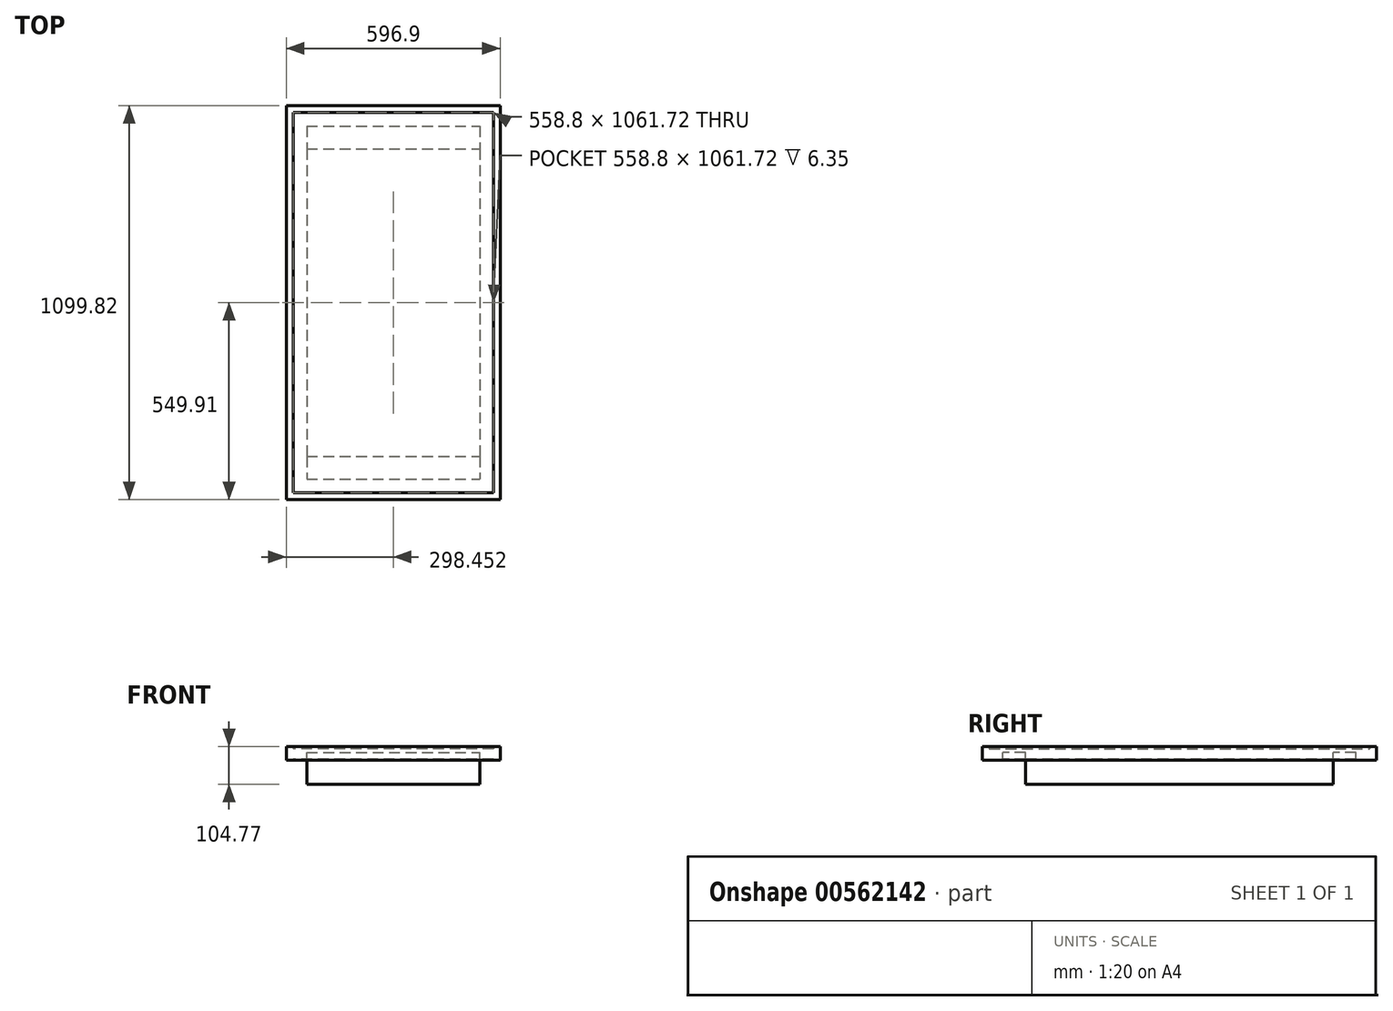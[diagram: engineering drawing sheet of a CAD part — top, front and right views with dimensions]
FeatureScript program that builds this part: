
annotation { "Feature Type Name" : "Feature", "Feature Type Description" : "" }
export const myFeature = defineFeature(function(context is Context, id is Id, definition is map)
    precondition{}
    {
        {
            var Q0;
            Q0=qCreatedBy(makeId("Top.planeOp"),FACE);
            var sketch = newSketch(context, id + "F0", { "sketchPlane" : qUnion([Q0])});
            skLineSegment(sketch, "E0.bottom", {"start": v(-98.88, 1025.28) * mm, "end": v(498.02, 1025.28) * mm});
            skLineSegment(sketch, "E0.top", {"start": v(-98.88, -74.54) * mm, "end": v(498.02, -74.54) * mm});
            skLineSegment(sketch, "E0.left", {"start": v(-98.88, 1025.28) * mm, "end": v(-98.88, -74.54) * mm});
            skLineSegment(sketch, "E0.right", {"start": v(498.02, 1025.28) * mm, "end": v(498.02, -74.54) * mm});
            skLineSegment(sketch, "E1.bottom", {"start": v(-79.83, 1006.23) * mm, "end": v(478.97, 1006.23) * mm});
            skLineSegment(sketch, "E1.top", {"start": v(-79.83, -55.5) * mm, "end": v(478.97, -55.5) * mm});
            skLineSegment(sketch, "E1.left", {"start": v(-79.83, 1006.23) * mm, "end": v(-79.83, -55.5) * mm});
            skLineSegment(sketch, "E1.right", {"start": v(478.97, 1006.23) * mm, "end": v(478.97, -55.5) * mm});
            skSolve(sketch);
        }
        {
            var Q0;
            Q0=makeQuery(id+"F0.imprint","IMPRINT",FACE,{"disambiguationData":[TD([[makeQuery(id+"F0.imprint","IMPRINT",EDGE,{"derivedFrom":sQuery(id+"F0.wireOp",EDGE,"E0.bottom")}),-1.0]])]});
            extrude(context, id + "F1", {"entities" : qUnion([Q0]), "depth" : 38.1 * mm, "offsetDistance" : 25.4 * mm});
        }
        {
            var Q0;
            Q0=makeQuery(id+"F1.opExtrude","SWEPT_FACE",FACE,{"disambiguationData":[OSD([sQuery(id+"F0.wireOp",EDGE,"E0.left")])]});
            var sketch = newSketch(context, id + "F2", { "sketchPlane" : qUnion([Q0])});
            skLineSegment(sketch, "E2.bottom", {"start": v(-1025.28, 31.75) * mm, "end": v(74.54, 31.75) * mm});
            skLineSegment(sketch, "E2.top", {"start": v(-1025.28, 22.23) * mm, "end": v(74.54, 22.23) * mm});
            skLineSegment(sketch, "E2.left", {"start": v(-1025.28, 31.75) * mm, "end": v(-1025.28, 22.23) * mm});
            skLineSegment(sketch, "E2.right", {"start": v(74.54, 31.75) * mm, "end": v(74.54, 22.23) * mm});
            skSolve(sketch);
        }
        {
            var Q0;
            Q0 = qSketchRegion(id + "F2", true);
            extrude(context, id + "F3", {"entities" : qUnion([Q0]), "operationType" : NewBodyOperationType.ADD, "oppositeDirection" : true, "depth" : 584.2 * mm, "offsetDistance" : 25.4 * mm});
        }
        {
            var Q0;
            Q0=makeQuery(id+"F3.opExtrude","SWEPT_FACE",FACE,{"disambiguationData":[OSD([sQuery(id+"F2.wireOp",EDGE,"E2.top")])]});
            var sketch = newSketch(context, id + "F4", { "sketchPlane" : qUnion([Q0])});
            skLineSegment(sketch, "E3.bottom", {"start": v(-79.83, -1006.23) * mm, "end": v(478.97, -1006.23) * mm});
            skLineSegment(sketch, "E3.top", {"start": v(-79.83, 55.5) * mm, "end": v(478.97, 55.5) * mm});
            skLineSegment(sketch, "E3.left", {"start": v(-79.83, -1006.23) * mm, "end": v(-79.83, 55.5) * mm});
            skLineSegment(sketch, "E3.right", {"start": v(478.97, -1006.23) * mm, "end": v(478.97, 55.5) * mm});
            skLineSegment(sketch, "E4.bottom", {"start": v(-41.73, -968.13) * mm, "end": v(440.87, -968.13) * mm});
            skLineSegment(sketch, "E4.top", {"start": v(-41.73, 17.4) * mm, "end": v(440.87, 17.4) * mm});
            skLineSegment(sketch, "E4.left", {"start": v(-41.73, -968.13) * mm, "end": v(-41.73, 17.4) * mm});
            skLineSegment(sketch, "E4.right", {"start": v(440.87, -968.13) * mm, "end": v(440.87, 17.4) * mm});
            skLineSegment(sketch, "E5.bottom", {"start": v(-41.73, -904.63) * mm, "end": v(440.87, -904.63) * mm});
            skLineSegment(sketch, "E5.top", {"start": v(-41.73, -866.53) * mm, "end": v(440.87, -866.53) * mm});
            skLineSegment(sketch, "E5.left", {"start": v(-41.73, -904.63) * mm, "end": v(-41.73, -866.53) * mm});
            skLineSegment(sketch, "E5.right", {"start": v(440.87, -904.63) * mm, "end": v(440.87, -866.53) * mm});
            skLineSegment(sketch, "E6.bottom", {"start": v(-41.73, -84.2) * mm, "end": v(440.87, -84.2) * mm});
            skLineSegment(sketch, "E6.top", {"start": v(-41.73, -46.1) * mm, "end": v(440.87, -46.1) * mm});
            skLineSegment(sketch, "E6.left", {"start": v(-41.73, -84.2) * mm, "end": v(-41.73, -46.1) * mm});
            skLineSegment(sketch, "E6.right", {"start": v(440.87, -84.2) * mm, "end": v(440.87, -46.1) * mm});
            skSolve(sketch);
        }
        {
            var Q0;
            Q0=makeQuery(id+"F4.imprint","IMPRINT",FACE,{"disambiguationData":[TD([[makeQuery(id+"F4.imprint","IMPRINT",EDGE,{"derivedFrom":sQuery(id+"F4.wireOp",EDGE,"E3.bottom")}),-1.0]])]});
            extrude(context, id + "F5", {"entities" : qUnion([Q0]), "operationType" : NewBodyOperationType.ADD, "depth" : 19.05 * mm, "offsetDistance" : 25.4 * mm});
        }
        {
            var Q0;
            Q0=makeQuery(id+"F3.opExtrude","SWEPT_FACE",FACE,{"disambiguationData":[OSD([sQuery(id+"F2.wireOp",EDGE,"E2.top")])]});
            var sketch = newSketch(context, id + "F6", { "sketchPlane" : qUnion([Q0])});
            skLineSegment(sketch, "E7.bottom", {"start": v(-41.73, -904.63) * mm, "end": v(440.87, -904.63) * mm});
            skLineSegment(sketch, "E7.top", {"start": v(-41.73, -866.53) * mm, "end": v(440.87, -866.53) * mm});
            skLineSegment(sketch, "E7.left", {"start": v(-41.73, -904.63) * mm, "end": v(-41.73, -866.53) * mm});
            skLineSegment(sketch, "E7.right", {"start": v(440.87, -904.63) * mm, "end": v(440.87, -866.53) * mm});
            skLineSegment(sketch, "E8.bottom", {"start": v(-41.73, -84.2) * mm, "end": v(440.87, -84.2) * mm});
            skLineSegment(sketch, "E8.top", {"start": v(-41.73, -46.1) * mm, "end": v(440.87, -46.1) * mm});
            skLineSegment(sketch, "E8.left", {"start": v(-41.73, -84.2) * mm, "end": v(-41.73, -46.1) * mm});
            skLineSegment(sketch, "E8.right", {"start": v(440.87, -84.2) * mm, "end": v(440.87, -46.1) * mm});
            skSolve(sketch);
        }
        {
            var Q0;
            Q0 = qSketchRegion(id + "F6", true);
            var Q1;
            {var subQ0=sQuery(id+"F6.wireOp",EDGE,"E7.top");Q1=makeQuery(id+"F6.imprint","IMPRINT",FACE,{"disambiguationData":[TD([[makeQuery(id+"F6.imprint","IMPRINT",EDGE,{"derivedFrom":subQ0}),1.0]])]});}
            extrude(context, id + "F7", {"entities" : qUnion([Q0, Q1]), "operationType" : NewBodyOperationType.ADD, "depth" : 88.9 * mm, "offsetDistance" : 25.4 * mm});
        }
    });
